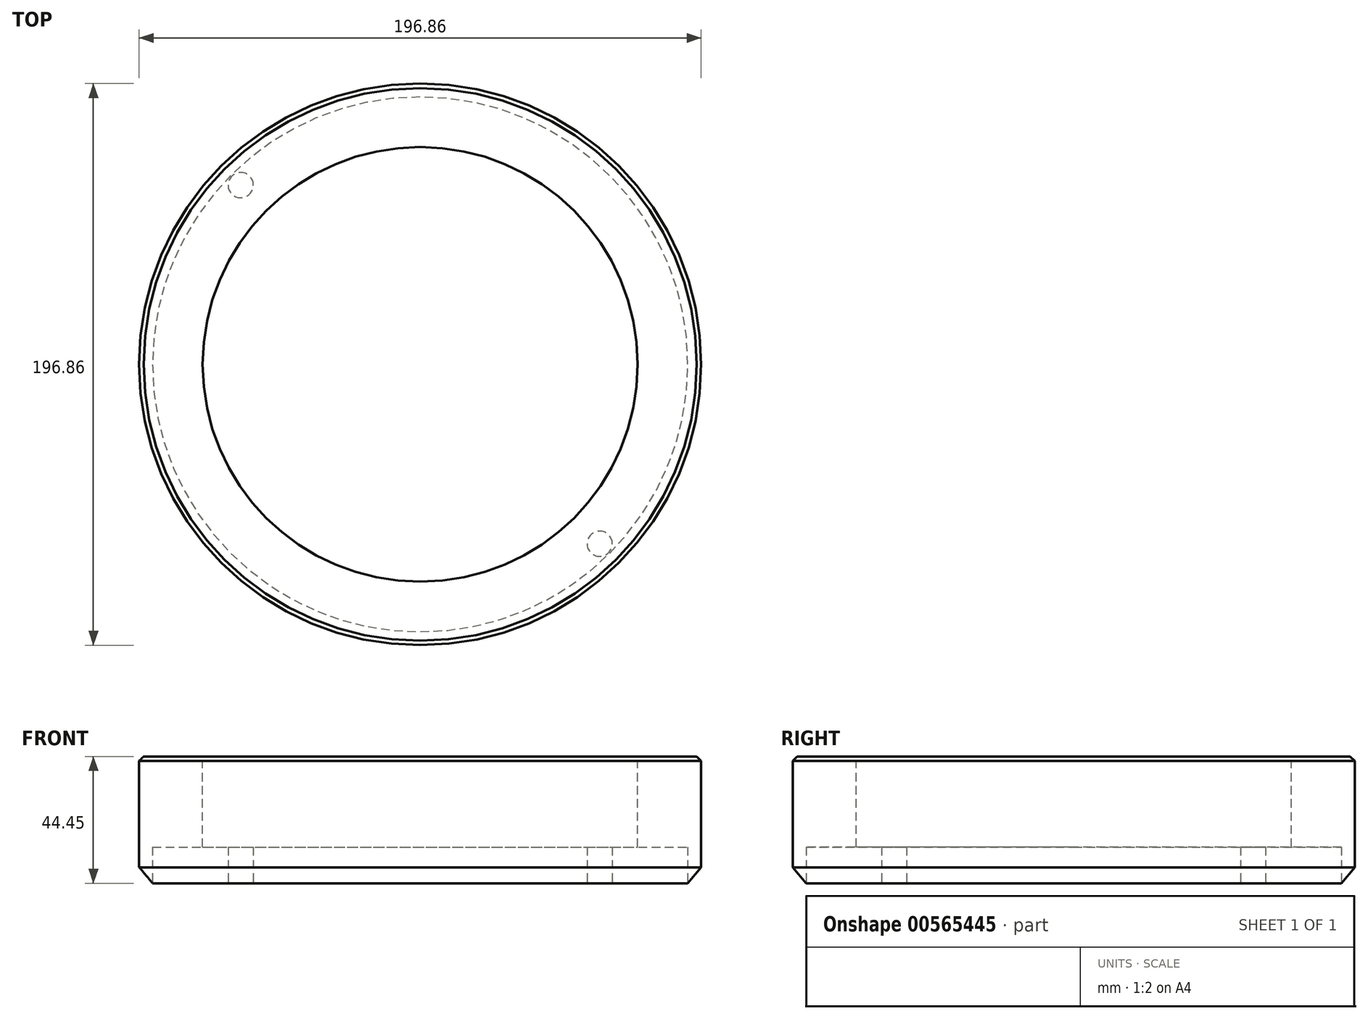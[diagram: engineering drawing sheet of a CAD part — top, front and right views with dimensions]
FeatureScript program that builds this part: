
annotation { "Feature Type Name" : "Feature", "Feature Type Description" : "" }
export const myFeature = defineFeature(function(context is Context, id is Id, definition is map)
    precondition{}
    {
        {
            var Q0;
            Q0=qCreatedBy(makeId("Front.planeOp"),FACE);
            var sketch = newSketch(context, id + "F0", { "sketchPlane" : qUnion([Q0])});
            skLineSegment(sketch, "E0", {"start": v(0, 0) * mm, "end": v(98.43, 0) * mm});
            skLineSegment(sketch, "E1", {"start": v(98.43, 0) * mm, "end": v(98.43, -38.85) * mm});
            skLineSegment(sketch, "E2", {"start": v(98.43, -38.85) * mm, "end": v(93.73, -44.45) * mm});
            skLineSegment(sketch, "E3", {"start": v(93.73, -44.45) * mm, "end": v(0, -44.45) * mm});
            skLineSegment(sketch, "E4", {"start": v(0, -44.45) * mm, "end": v(0, 0) * mm});
            skSolve(sketch);
        }
        {
            var Q0;
            Q0 = qSketchRegion(id + "F0", true);
            var Q1;
            Q1=sQuery(id+"F0.wireOp",EDGE,"E4");
            revolve(context, id + "F1", {"entities" : qUnion([Q0]), "axis" : qUnion([Q1]), "revolveType" : RevolveType.FULL});
        }
        {
            var Q0;
            Q0=makeQuery(id+"F1.opRevolve","SWEPT_EDGE",EDGE,{"disambiguationData":[OSD([sQuery(id+"F0.wireOp",EDGE,"E0"),sQuery(id+"F0.wireOp",EDGE,"E1")])]});
            chamfer(context, id + "F2", {"entities" : qUnion([Q0]), "chamferType" : ChamferType.OFFSET_ANGLE, "width" : 1.57 * mm, "oppositeDirection" : false, "angle" : 45 * degree, "tangentPropagation" : true});
        }
        {
            var Q0;
            Q0=makeQuery(id+"F1.opRevolve","SWEPT_FACE",FACE,{"disambiguationData":[OSD([sQuery(id+"F0.wireOp",EDGE,"E3")])]});
            var sketch = newSketch(context, id + "F3", { "sketchPlane" : qUnion([Q0])});
            skLineSegment(sketch, "E5", {"start": v(-173.3, 0) * mm, "end": v(188.3, 0) * mm, "construction": true});
            skLineSegment(sketch, "E6", {"start": v(0, 128.5) * mm, "end": v(0, -161.91) * mm, "construction": true});
            skLineSegment(sketch, "E7", {"start": v(0, 0) * mm, "end": v(44.02, -164.29) * mm, "construction": true});
            skCircle(sketch, "E8", {"center": v(0, 0) * mm, "radius": 88.9 * mm});
            skCircle(sketch, "E9", {"center": v(23, -85.87) * mm, "radius": 4.42 * mm});
            skCircle(sketch, "E10.1.0", {"center": v(85.87, -23) * mm, "radius": 4.42 * mm});
            skCircle(sketch, "E10.2.0", {"center": v(62.86, 62.86) * mm, "radius": 4.42 * mm});
            skCircle(sketch, "E10.3.0", {"center": v(-23, 85.87) * mm, "radius": 4.42 * mm});
            skCircle(sketch, "E10.4.0", {"center": v(-85.87, 23) * mm, "radius": 4.42 * mm});
            skCircle(sketch, "E10.5.0", {"center": v(-62.86, -62.86) * mm, "radius": 4.42 * mm});
            skSolve(sketch);
        }
        {
            var Q0;
            {var subQ0=sQuery(id+"F3.wireOp",EDGE,"E10.3.0");var subQ1=sQuery(id+"F3.wireOp",EDGE,"E8");var subQ2=makeQuery(id+"F3.imprint","INTERSECT",VERTEX,{"disambiguationData":[OD(0.0)],"derivedFrom":[subQ1,subQ0]});Q0=makeQuery(id+"F3.imprint","IMPRINT",FACE,{"disambiguationData":[TD([[makeQuery(id+"F3.imprint","IMPRINT",EDGE,{"disambiguationData":[TD([[subQ2,-1.0]])],"derivedFrom":subQ1}),1.0]])]});}
            var Q1;
            {var subQ0=sQuery(id+"F3.wireOp",EDGE,"E10.3.0");var subQ1=sQuery(id+"F3.wireOp",EDGE,"E8");var subQ2=makeQuery(id+"F3.imprint","INTERSECT",VERTEX,{"disambiguationData":[OD(0.0)],"derivedFrom":[subQ1,subQ0]});Q1=makeQuery(id+"F3.imprint","IMPRINT",FACE,{"disambiguationData":[TD([[makeQuery(id+"F3.imprint","IMPRINT",EDGE,{"disambiguationData":[TD([[subQ2,-1.0]])],"derivedFrom":subQ1}),-1.0]])]});}
            var Q2;
            {var subQ0=sQuery(id+"F3.wireOp",EDGE,"E10.2.0");var subQ1=sQuery(id+"F3.wireOp",EDGE,"E8");var subQ2=makeQuery(id+"F3.imprint","INTERSECT",VERTEX,{"disambiguationData":[OD(0.0)],"derivedFrom":[subQ1,subQ0]});Q2=makeQuery(id+"F3.imprint","IMPRINT",FACE,{"disambiguationData":[TD([[makeQuery(id+"F3.imprint","IMPRINT",EDGE,{"disambiguationData":[TD([[subQ2,1.0]])],"derivedFrom":subQ1}),-1.0]])]});}
            var Q3;
            {var subQ0=sQuery(id+"F3.wireOp",EDGE,"E10.2.0");var subQ1=sQuery(id+"F3.wireOp",EDGE,"E8");var subQ2=makeQuery(id+"F3.imprint","INTERSECT",VERTEX,{"disambiguationData":[OD(0.0)],"derivedFrom":[subQ1,subQ0]});Q3=makeQuery(id+"F3.imprint","IMPRINT",FACE,{"disambiguationData":[TD([[makeQuery(id+"F3.imprint","IMPRINT",EDGE,{"disambiguationData":[TD([[subQ2,1.0]])],"derivedFrom":subQ1}),1.0]])]});}
            var Q4;
            {var subQ0=sQuery(id+"F3.wireOp",EDGE,"E10.4.0");var subQ1=sQuery(id+"F3.wireOp",EDGE,"E8");var subQ2=makeQuery(id+"F3.imprint","INTERSECT",VERTEX,{"disambiguationData":[OD(0.0)],"derivedFrom":[subQ1,subQ0]});Q4=makeQuery(id+"F3.imprint","IMPRINT",FACE,{"disambiguationData":[TD([[makeQuery(id+"F3.imprint","IMPRINT",EDGE,{"disambiguationData":[TD([[subQ2,-1.0]])],"derivedFrom":subQ1}),-1.0]])]});}
            var Q5;
            {var subQ0=sQuery(id+"F3.wireOp",EDGE,"E10.4.0");var subQ1=sQuery(id+"F3.wireOp",EDGE,"E8");var subQ2=makeQuery(id+"F3.imprint","INTERSECT",VERTEX,{"disambiguationData":[OD(0.0)],"derivedFrom":[subQ1,subQ0]});Q5=makeQuery(id+"F3.imprint","IMPRINT",FACE,{"disambiguationData":[TD([[makeQuery(id+"F3.imprint","IMPRINT",EDGE,{"disambiguationData":[TD([[subQ2,-1.0]])],"derivedFrom":subQ1}),1.0]])]});}
            var Q6;
            {var subQ0=sQuery(id+"F3.wireOp",EDGE,"E10.5.0");var subQ1=sQuery(id+"F3.wireOp",EDGE,"E8");var subQ2=makeQuery(id+"F3.imprint","INTERSECT",VERTEX,{"disambiguationData":[OD(0.0)],"derivedFrom":[subQ1,subQ0]});Q6=makeQuery(id+"F3.imprint","IMPRINT",FACE,{"disambiguationData":[TD([[makeQuery(id+"F3.imprint","IMPRINT",EDGE,{"disambiguationData":[TD([[subQ2,-1.0]])],"derivedFrom":subQ1}),1.0]])]});}
            var Q7;
            {var subQ0=sQuery(id+"F3.wireOp",EDGE,"E10.5.0");var subQ1=sQuery(id+"F3.wireOp",EDGE,"E8");var subQ2=makeQuery(id+"F3.imprint","INTERSECT",VERTEX,{"disambiguationData":[OD(0.0)],"derivedFrom":[subQ1,subQ0]});Q7=makeQuery(id+"F3.imprint","IMPRINT",FACE,{"disambiguationData":[TD([[makeQuery(id+"F3.imprint","IMPRINT",EDGE,{"disambiguationData":[TD([[subQ2,-1.0]])],"derivedFrom":subQ1}),-1.0]])]});}
            var Q8;
            {var subQ0=sQuery(id+"F3.wireOp",EDGE,"E9");var subQ1=sQuery(id+"F3.wireOp",EDGE,"E8");var subQ2=makeQuery(id+"F3.imprint","INTERSECT",VERTEX,{"disambiguationData":[OD(0.0)],"derivedFrom":[subQ1,subQ0]});Q8=makeQuery(id+"F3.imprint","IMPRINT",FACE,{"disambiguationData":[TD([[makeQuery(id+"F3.imprint","IMPRINT",EDGE,{"disambiguationData":[TD([[subQ2,-1.0]])],"derivedFrom":subQ1}),1.0]])]});}
            var Q9;
            {var subQ0=sQuery(id+"F3.wireOp",EDGE,"E9");var subQ1=sQuery(id+"F3.wireOp",EDGE,"E8");var subQ2=makeQuery(id+"F3.imprint","INTERSECT",VERTEX,{"disambiguationData":[OD(0.0)],"derivedFrom":[subQ1,subQ0]});Q9=makeQuery(id+"F3.imprint","IMPRINT",FACE,{"disambiguationData":[TD([[makeQuery(id+"F3.imprint","IMPRINT",EDGE,{"disambiguationData":[TD([[subQ2,-1.0]])],"derivedFrom":subQ1}),-1.0]])]});}
            var Q10;
            {var subQ0=sQuery(id+"F3.wireOp",EDGE,"E10.1.0");var subQ1=sQuery(id+"F3.wireOp",EDGE,"E8");var subQ2=makeQuery(id+"F3.imprint","INTERSECT",VERTEX,{"disambiguationData":[OD(0.0)],"derivedFrom":[subQ1,subQ0]});Q10=makeQuery(id+"F3.imprint","IMPRINT",FACE,{"disambiguationData":[TD([[makeQuery(id+"F3.imprint","IMPRINT",EDGE,{"disambiguationData":[TD([[subQ2,-1.0]])],"derivedFrom":subQ1}),1.0]])]});}
            var Q11;
            {var subQ0=sQuery(id+"F3.wireOp",EDGE,"E10.1.0");var subQ1=sQuery(id+"F3.wireOp",EDGE,"E8");var subQ2=makeQuery(id+"F3.imprint","INTERSECT",VERTEX,{"disambiguationData":[OD(0.0)],"derivedFrom":[subQ1,subQ0]});Q11=makeQuery(id+"F3.imprint","IMPRINT",FACE,{"disambiguationData":[TD([[makeQuery(id+"F3.imprint","IMPRINT",EDGE,{"disambiguationData":[TD([[subQ2,-1.0]])],"derivedFrom":subQ1}),-1.0]])]});}
            var Q12;
            Q12=sQuery(id+"F3.wireOp",EDGE,"E10.3.0");
            var Q13;
            Q13=sQuery(id+"F3.wireOp",EDGE,"E10.4.0");
            var Q14;
            Q14=sQuery(id+"F3.wireOp",EDGE,"E10.2.0");
            var Q15;
            Q15=sQuery(id+"F3.wireOp",EDGE,"E10.1.0");
            var Q16;
            Q16=sQuery(id+"F3.wireOp",EDGE,"E9");
            var Q17;
            Q17=sQuery(id+"F3.wireOp",EDGE,"E10.5.0");
            extrude(context, id + "F4", {"entities" : qUnion([Q0, Q1, Q2, Q3, Q4, Q5, Q6, Q7, Q8, Q9, Q10, Q11]), "operationType" : NewBodyOperationType.REMOVE, "surfaceEntities" : qUnion([Q12, Q13, Q14, Q15, Q16, Q17]), "oppositeDirection" : true, "depth" : 12.7 * mm, "offsetDistance" : 25.4 * mm});
        }
        {
            var Q0;
            Q0=makeQuery(id+"F1.opRevolve","SWEPT_FACE",FACE,{"disambiguationData":[OSD([sQuery(id+"F0.wireOp",EDGE,"E0")])]});
            var sketch = newSketch(context, id + "F5", { "sketchPlane" : qUnion([Q0])});
            skCircle(sketch, "E11", {"center": v(0, 0) * mm, "radius": 76.2 * mm});
            skSolve(sketch);
        }
        {
            var Q0;
            Q0 = qSketchRegion(id + "F5", true);
            extrude(context, id + "F6", {"entities" : qUnion([Q0]), "operationType" : NewBodyOperationType.REMOVE, "endBound" : BoundingType.THROUGH_ALL, "oppositeDirection" : true, "depth" : 25.4 * mm, "offsetDistance" : 25.4 * mm});
        }
    });
